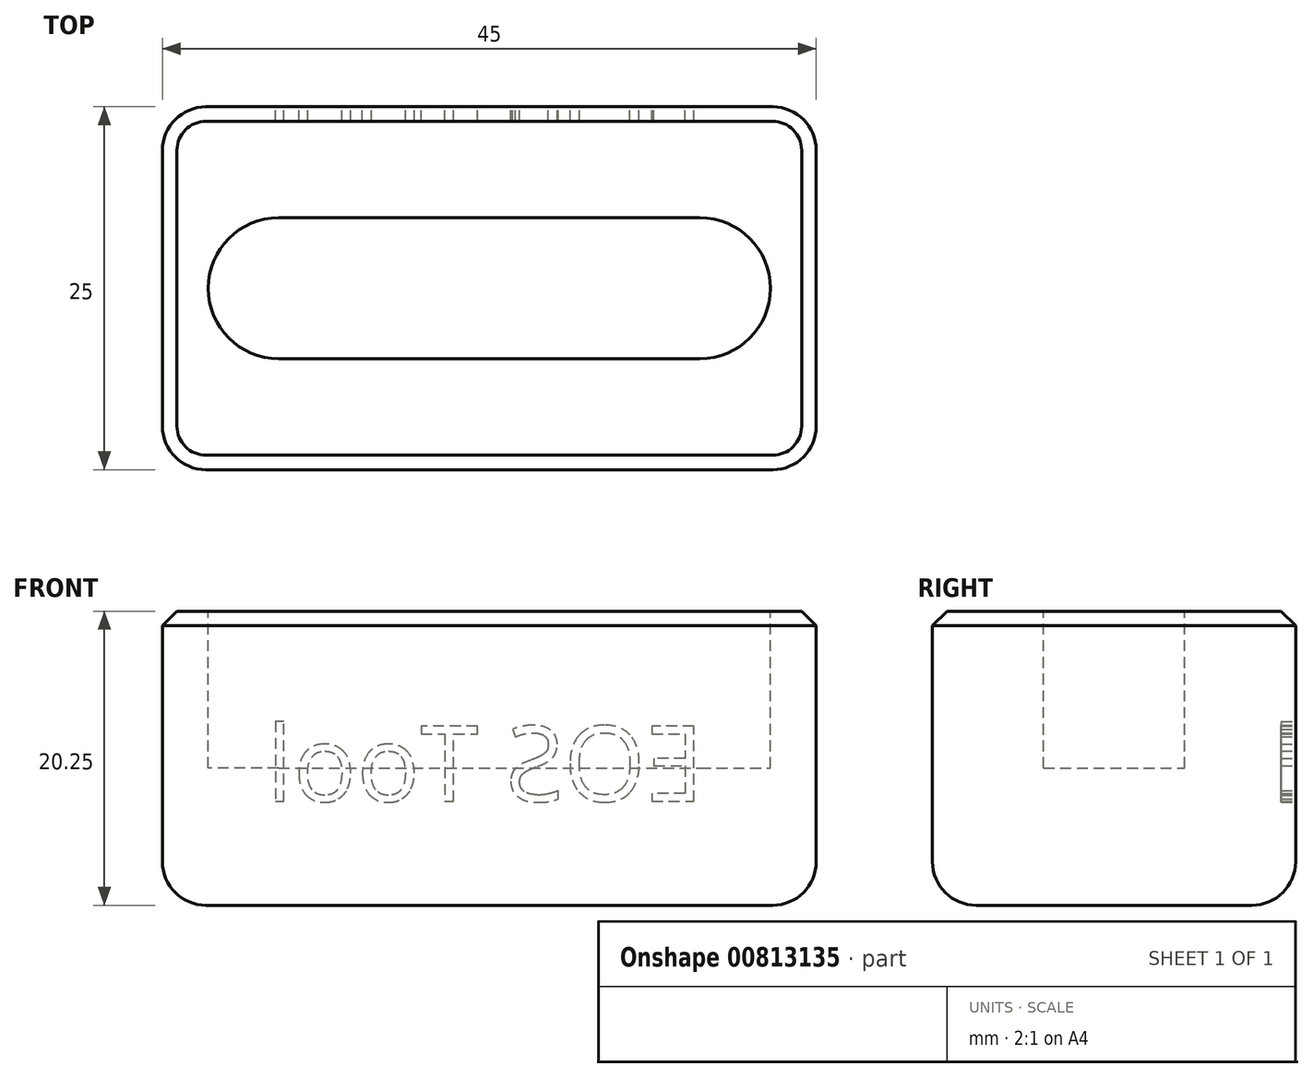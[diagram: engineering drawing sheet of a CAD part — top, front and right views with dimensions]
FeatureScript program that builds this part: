
annotation { "Feature Type Name" : "Feature", "Feature Type Description" : "" }
export const myFeature = defineFeature(function(context is Context, id is Id, definition is map)
    precondition{}
    {
        {
            var Q0;
            Q0=qCreatedBy(makeId("Top.planeOp"),FACE);
            var sketch = newSketch(context, id + "F0", { "sketchPlane" : qUnion([Q0])});
            skLineSegment(sketch, "E0.bottom", {"start": v(-22.5, 12.5) * mm, "end": v(22.5, 12.5) * mm});
            skLineSegment(sketch, "E0.top", {"start": v(-22.5, -12.5) * mm, "end": v(22.5, -12.5) * mm});
            skLineSegment(sketch, "E0.left", {"start": v(-22.5, 12.5) * mm, "end": v(-22.5, -12.5) * mm});
            skLineSegment(sketch, "E0.right", {"start": v(22.5, 12.5) * mm, "end": v(22.5, -12.5) * mm});
            skSolve(sketch);
        }
        {
            var Q0;
            Q0=makeQuery(id+"F0.imprint","IMPRINT",FACE,{"disambiguationData":[TD([[makeQuery(id+"F0.imprint","IMPRINT",EDGE,{"derivedFrom":sQuery(id+"F0.wireOp",EDGE,"E0.bottom")}),-1.0]])]});
            extrude(context, id + "F1", {"entities" : qUnion([Q0]), "depth" : 20.25 * mm, "offsetDistance" : 25 * mm});
        }
        {
            var Q0;
            Q0=makeQuery(id+"F1.opExtrude","CAP_FACE",FACE,{"disambiguationData":[OSD([sQuery(id+"F0.wireOp",EDGE,"E0.bottom"),sQuery(id+"F0.wireOp",EDGE,"E0.top"),sQuery(id+"F0.wireOp",EDGE,"E0.left"),sQuery(id+"F0.wireOp",EDGE,"E0.right")])],"isStart":false});
            var sketch = newSketch(context, id + "F2", { "sketchPlane" : qUnion([Q0])});
            skLineSegment(sketch, "E1.bottom", {"start": v(-14.5, 4.85) * mm, "end": v(14.5, 4.85) * mm});
            skLineSegment(sketch, "E1.top", {"start": v(-14.5, -4.85) * mm, "end": v(14.5, -4.85) * mm});
            skLineSegment(sketch, "E1.left", {"start": v(-19.35, 0) * mm, "end": v(-19.35, 0) * mm});
            skLineSegment(sketch, "E1.right", {"start": v(19.35, 0) * mm, "end": v(19.35, 0) * mm});
            skPoint(sketch, "E2.visualSharp", {"position": v(19.35, 4.85) * mm});
            skArc(sketch, "E2.filletArc", {"start": v(19.35, 0) * mm, "mid": v(17.93, 3.43) * mm, "end": v(14.5, 4.85) * mm});
            skPoint(sketch, "E3.visualSharp", {"position": v(19.35, -4.85) * mm});
            skArc(sketch, "E3.filletArc", {"start": v(14.5, -4.85) * mm, "mid": v(17.93, -3.43) * mm, "end": v(19.35, 0) * mm});
            skPoint(sketch, "E4.visualSharp", {"position": v(-19.35, 4.85) * mm});
            skArc(sketch, "E4.filletArc", {"start": v(-14.5, 4.85) * mm, "mid": v(-17.93, 3.43) * mm, "end": v(-19.35, 0) * mm});
            skPoint(sketch, "E5.visualSharp", {"position": v(-19.35, -4.85) * mm});
            skArc(sketch, "E5.filletArc", {"start": v(-19.35, 0) * mm, "mid": v(-17.93, -3.43) * mm, "end": v(-14.5, -4.85) * mm});
            skSolve(sketch);
        }
        {
            var Q0;
            Q0=makeQuery(id+"F2.imprint","IMPRINT",FACE,{"disambiguationData":[TD([[makeQuery(id+"F2.imprint","IMPRINT",EDGE,{"derivedFrom":sQuery(id+"F2.wireOp",EDGE,"E1.bottom")}),-1.0]])]});
            extrude(context, id + "F3", {"entities" : qUnion([Q0]), "operationType" : NewBodyOperationType.REMOVE, "oppositeDirection" : true, "depth" : 10.8 * mm, "offsetDistance" : 25 * mm});
        }
        {
            var Q0;
            Q0=makeQuery(id+"F1.opExtrude","CAP_EDGE",EDGE,{"disambiguationData":[OSD([sQuery(id+"F0.wireOp",EDGE,"E0.left")])],"isStart":true});
            var Q1;
            Q1=makeQuery(id+"F1.opExtrude","CAP_EDGE",EDGE,{"disambiguationData":[OSD([sQuery(id+"F0.wireOp",EDGE,"E0.top")])],"isStart":true});
            var Q2;
            Q2=makeQuery(id+"F1.opExtrude","CAP_EDGE",EDGE,{"disambiguationData":[OSD([sQuery(id+"F0.wireOp",EDGE,"E0.bottom")])],"isStart":true});
            var Q3;
            Q3=makeQuery(id+"F1.opExtrude","CAP_EDGE",EDGE,{"disambiguationData":[OSD([sQuery(id+"F0.wireOp",EDGE,"E0.right")])],"isStart":true});
            var Q4;
            Q4=makeQuery(id+"F1.opExtrude","SWEPT_EDGE",EDGE,{"disambiguationData":[OSD([sQuery(id+"F0.wireOp",EDGE,"E0.bottom"),sQuery(id+"F0.wireOp",EDGE,"E0.right")])]});
            var Q5;
            Q5=makeQuery(id+"F1.opExtrude","SWEPT_EDGE",EDGE,{"disambiguationData":[OSD([sQuery(id+"F0.wireOp",EDGE,"E0.top"),sQuery(id+"F0.wireOp",EDGE,"E0.right")])]});
            var Q6;
            Q6=makeQuery(id+"F1.opExtrude","SWEPT_EDGE",EDGE,{"disambiguationData":[OSD([sQuery(id+"F0.wireOp",EDGE,"E0.top"),sQuery(id+"F0.wireOp",EDGE,"E0.left")])]});
            var Q7;
            Q7=makeQuery(id+"F1.opExtrude","SWEPT_EDGE",EDGE,{"disambiguationData":[OSD([sQuery(id+"F0.wireOp",EDGE,"E0.bottom"),sQuery(id+"F0.wireOp",EDGE,"E0.left")])]});
            fillet(context, id + "F4", {"entities" : qUnion([Q0, Q1, Q2, Q3, Q4, Q5, Q6, Q7]), "radius" : 3 * mm, "tangentPropagation" : true, "allowEdgeOverflow" : false});
        }
        {
            var Q0;
            Q0=makeQuery(id+"F1.opExtrude","CAP_EDGE",EDGE,{"disambiguationData":[OSD([sQuery(id+"F0.wireOp",EDGE,"E0.top")])],"isStart":false});
            var Q1;
            Q1=makeQuery(id+"F3.boolean.opBoolean","COPY",EDGE,{"derivedFrom":makeQuery(id+"F3.opExtrude","CAP_EDGE",EDGE,{"disambiguationData":[OSD([sQuery(id+"F2.wireOp",EDGE,"E2.filletArc"),sQuery(id+"F2.wireOp",EDGE,"E3.filletArc")])],"isStart":true})});
            chamfer(context, id + "F5", {"entities" : qUnion([Q0, Q1]), "width" : 1 * mm, "tangentPropagation" : true});
        }
        {
            var Q0;
            Q0=makeQuery(id+"F1.opExtrude","SWEPT_FACE",FACE,{"disambiguationData":[OSD([sQuery(id+"F0.wireOp",EDGE,"E0.bottom")])]});
            var sketch = newSketch(context, id + "F6", { "sketchPlane" : qUnion([Q0])});
            skText(sketch, "E6", { "text": "EOS Tool", "fontName": "OpenSans-Regular.ttf"});
            const initialGuessF6  = {"E6": [-0.01479, 0.00716, 1, 0, 0.00522]};
            skSetInitialGuess(sketch, initialGuessF6);
            skSolve(sketch);
        }
        {
            var Q0;
            Q0 = qSketchRegion(id + "F6", true);
            extrude(context, id + "F7", {"entities" : qUnion([Q0]), "operationType" : NewBodyOperationType.REMOVE, "oppositeDirection" : true, "depth" : 1 * mm, "offsetDistance" : 25 * mm});
        }
    });
